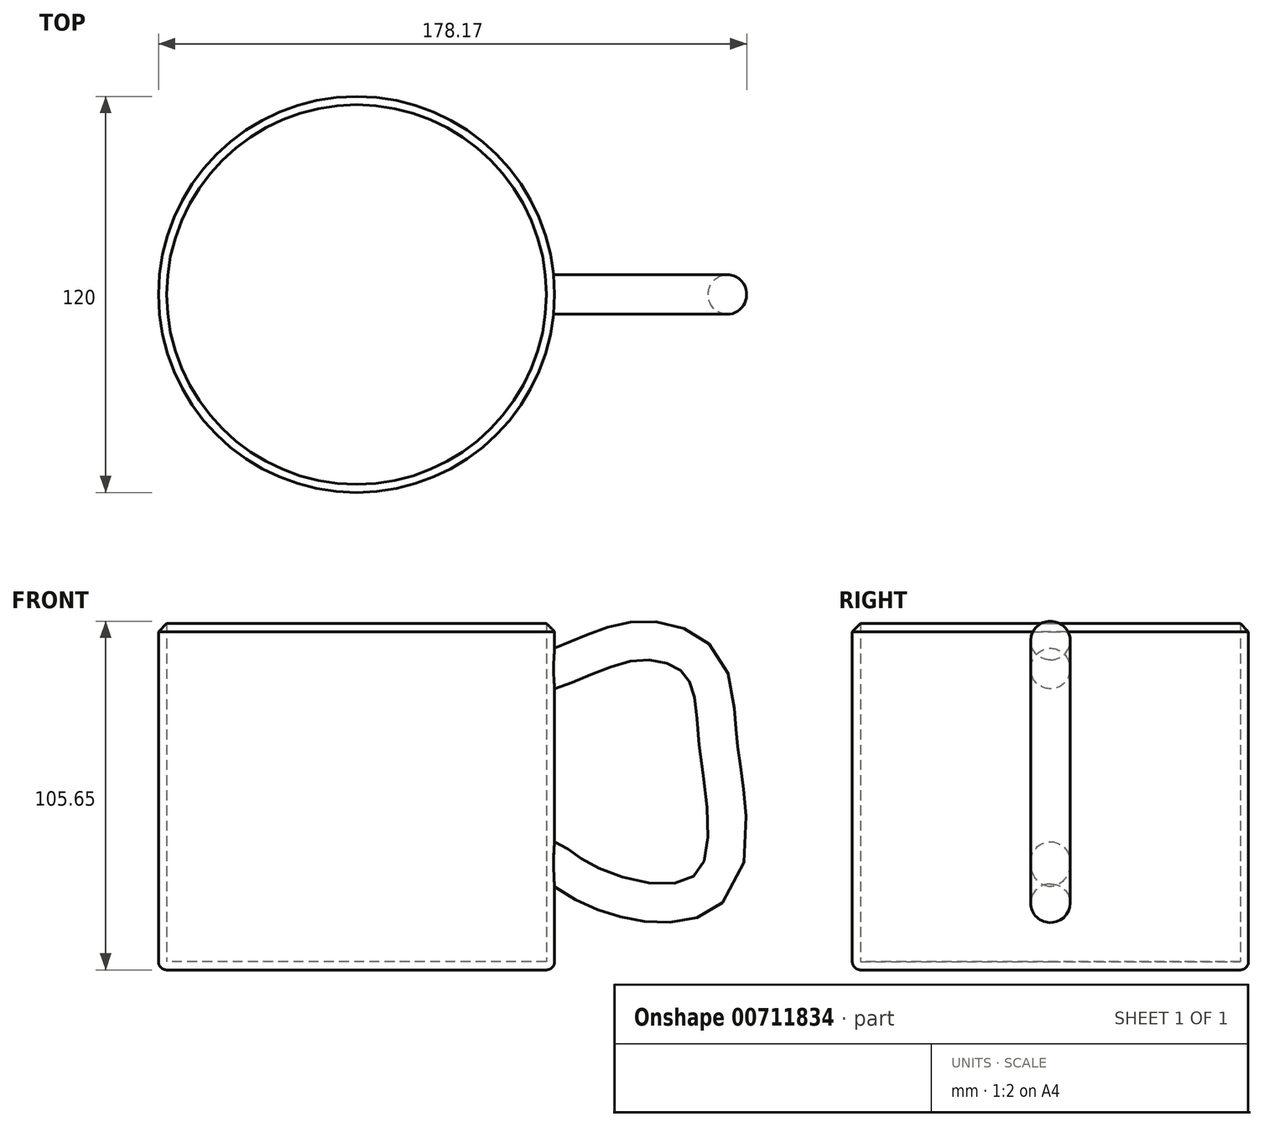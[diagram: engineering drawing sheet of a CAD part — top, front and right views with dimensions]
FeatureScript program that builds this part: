
annotation { "Feature Type Name" : "Feature", "Feature Type Description" : "" }
export const myFeature = defineFeature(function(context is Context, id is Id, definition is map)
    precondition{}
    {
        {
            var Q0;
            Q0=qCreatedBy(makeId("Top.planeOp"),FACE);
            var sketch = newSketch(context, id + "F0", { "sketchPlane" : qUnion([Q0])});
            skCircle(sketch, "E0", {"center": v(0, 0) * mm, "radius": 60 * mm});
            skSolve(sketch);
        }
        {
            var Q0;
            Q0 = qSketchRegion(id + "F0", true);
            extrude(context, id + "F1", {"entities" : qUnion([Q0]), "depth" : 105 * mm, "offsetDistance" : 25 * mm});
        }
        {
            var Q0;
            Q0=qCreatedBy(makeId("Right.planeOp"),FACE);
            cPlane(context, id + "F2", {"entities" : qUnion([Q0]), "cplaneType" : CPlaneType.OFFSET, "offset" : 51 * mm, "width" : 150 * mm, "height" : 150 * mm});
        }
        {
            var Q0;
            Q0=qCreatedBy(makeId("Front.planeOp"),FACE);
            var sketch = newSketch(context, id + "F3", { "sketchPlane" : qUnion([Q0])});
            skFitSpline(sketch, "E1", {"points": [v(50.81, 84.06) * mm, v(64.49, 88.35) * mm, v(85.67, 95.32) * mm, v(100.95, 89.96) * mm, v(105.24, 67.97) * mm, v(103.9, 28.02) * mm, v(73.07, 29.36) * mm, v(59.66, 37.4) * mm, v(51.08, 38.48) * mm], "startDerivative": vector(122.7, 32.4) * mm, "endDerivative": vector(-107.71, -0.66) * mm});
            skSolve(sketch);
        }
        {
            var Q0;
            Q0=qCreatedBy(id+"F2.planeOp",FACE);
            var sketch = newSketch(context, id + "F4", { "sketchPlane" : qUnion([Q0])});
            skCircle(sketch, "E2", {"center": v(0, 88.62) * mm, "radius": 6 * mm});
            skSolve(sketch);
        }
        {
            var Q0;
            Q0 = qSketchRegion(id + "F4", true);
            var Q1;
            Q1 = qConstructionFilter(qBodyType(qCreatedBy(id + "F3" ,EDGE), BodyType.WIRE), ConstructionObject.NO);
            sweep(context, id + "F5", {"operationType" : NewBodyOperationType.ADD, "profiles" : qUnion([Q0]), "path" : qUnion([Q1])});
        }
        {
            var Q0;
            Q0=makeQuery(id+"F1.opExtrude","CAP_FACE",FACE,{"disambiguationData":[OSD([sQuery(id+"F0.wireOp",EDGE,"E0")])],"isStart":false});
            shell(context, id + "F6", {"entities" : qUnion([Q0]), "thickness" : 2.5 * mm});
        }
        {
            var Q0;
            Q0=makeQuery(id+"F1.opExtrude","CAP_EDGE",EDGE,{"disambiguationData":[OSD([sQuery(id+"F0.wireOp",EDGE,"E0")])],"isStart":false});
            chamfer(context, id + "F7", {"entities" : qUnion([Q0]), "width" : 2.5 * mm, "tangentPropagation" : true});
        }
        {
            var Q0;
            Q0=makeQuery(id+"F1.opExtrude","CAP_FACE",FACE,{"disambiguationData":[OSD([sQuery(id+"F0.wireOp",EDGE,"E0")])],"isStart":true});
            fillet(context, id + "F8", {"entities" : qUnion([Q0]), "radius" : 2.5 * mm, "tangentPropagation" : true, "allowEdgeOverflow" : false});
        }
    });
